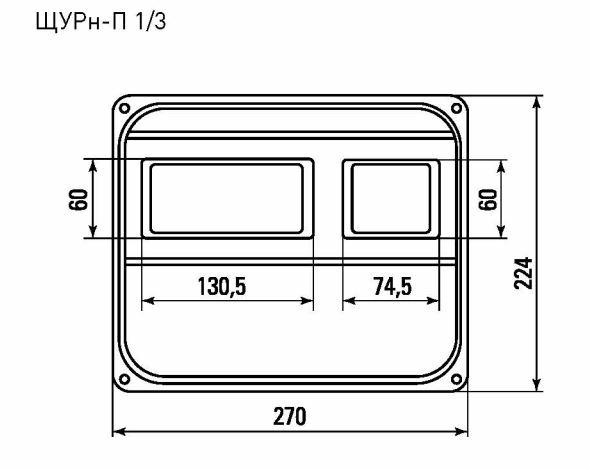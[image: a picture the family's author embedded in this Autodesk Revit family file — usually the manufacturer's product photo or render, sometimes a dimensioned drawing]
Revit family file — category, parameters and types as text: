
# Revit family: EKF_EE_ЦокольУсиленныйFORT_PROxima
name_source: partatom
category: Электрооборудование
units: mm (PartAtom-declared; Revit-internal decimal feet)

## family parameters
Всегда вертикально = Нет
На основе рабочей плоскости = Да
Общий = Да
При загрузке вырезать с полостями = Нет
Размер круглого соединителя = Использовать диаметр
Тип детали = Силовой щит
Точка расчета площади = Нет

## types (12) — shared parameters
ADSK_Единица измерения = шт.
ADSK_Завод-изготовитель = EKF
ADSK_Количество = 1
ADSK_Марка = Цоколь усиленный FORT
ADSK_Материал = RAL 7035_Сталь
ADSK_Обозначение = Цоколь усиленный FORT
ADSK_Размер_Высота = 100 мм
БезСальникПанели = Без сальниковой панели
Глубина = 400 мм
Изготовитель = EKF
КПЦ1000 = EKF_EE_КомплектПанелейЦоколя_FORT_PROxima : Комплект панелей цоколя FORT Ш1000 В200 PROxima (2шт)
КПЦ400 = EKF_EE_КомплектПанелейЦоколя_FORT_PROxima : Комплект панелей цоколя FORT Ш400 В200  PROxima (2шт)
КПЦ600 = EKF_EE_КомплектПанелейЦоколя_FORT_PROxima : Комплект панелей цоколя FORT Ш600 В200 PROxima (2шт)
КПЦ800 = EKF_EE_КомплектПанелейЦоколя_FORT_PROxima : Комплект панелей цоколя FORT  Ш800 В200 PROxima (2 шт)
СальникПанель = EKF_EE_НижняяСальниковаяПанельСоставнаяFORT_PROxima : Нижняя сальниковая панель составная FORT (800x600) EKF PROxima
Серия номенклатуры = PROxima
Степень защиты IP = -
ТВ = EKF_2
Тип установки = -
Ширина = 600 мм
zero-valued in all types: ADSK_Масса, Отметка по умолчанию

## per-type parameters (varying)
| type | ADSK_Код изделия | ADSK_Наименование | ADSK_Размер_Глубина | ADSK_Размер_Ширина | ПанелиЦоколя_Глубина | ПанелиЦоколя_Ширина | СальниковаяПанель | Тип |
| Цоколь усиленный FORT 1000х400 EKF PROxima | FCS104 | Цоколь усиленный FORT 1000х400 EKF PROxima | 400 мм | 1000 мм | EKF_EE_КомплектПанелейЦоколя_FORT_PROxima : Комплект панелей цоколя FORT Ш400 В200  PROxima (2шт) | EKF_EE_КомплектПанелейЦоколя_FORT_PROxima : Комплект панелей цоколя FORT Ш1000 В200 PROxima (2шт) | Без сальниковой панели | 348 мм |
| Цоколь усиленный FORT 1000х600 EKF PROxima | FCS106 | Цоколь усиленный FORT 1000х600 EKF PROxima | 600 мм | 1000 мм | EKF_EE_КомплектПанелейЦоколя_FORT_PROxima : Комплект панелей цоколя FORT Ш600 В200 PROxima (2шт) | EKF_EE_КомплектПанелейЦоколя_FORT_PROxima : Комплект панелей цоколя FORT Ш1000 В200 PROxima (2шт) | Без сальниковой панели | 349 мм |
| Цоколь усиленный FORT 1000х800 EKF PROxima | FCS108 | Цоколь усиленный FORT 1000х800 EKF PROxima | 800 мм | 1000 мм | EKF_EE_КомплектПанелейЦоколя_FORT_PROxima : Комплект панелей цоколя FORT  Ш800 В200 PROxima (2 шт) | EKF_EE_КомплектПанелейЦоколя_FORT_PROxima : Комплект панелей цоколя FORT Ш1000 В200 PROxima (2шт) | Без сальниковой панели | 350 мм |
| Цоколь усиленный FORT 400х400 EKF PROxima | FCS44 | Цоколь усиленный FORT 400х400 EKF PROxima | 400 мм | 400 мм | EKF_EE_КомплектПанелейЦоколя_FORT_PROxima : Комплект панелей цоколя FORT Ш400 В200  PROxima (2шт) | EKF_EE_КомплектПанелейЦоколя_FORT_PROxima : Комплект панелей цоколя FORT Ш400 В200  PROxima (2шт) | Без сальниковой панели | 351 мм |
| Цоколь усиленный FORT 400х600 EKF PROxima | FCS46 | Цоколь усиленный FORT 400х600 EKF PROxima | 600 мм | 400 мм | EKF_EE_КомплектПанелейЦоколя_FORT_PROxima : Комплект панелей цоколя FORT Ш600 В200 PROxima (2шт) | EKF_EE_КомплектПанелейЦоколя_FORT_PROxima : Комплект панелей цоколя FORT Ш400 В200  PROxima (2шт) | Без сальниковой панели | 352 мм |
| Цоколь усиленный FORT 400х800 EKF PROxima | FCS48 | Цоколь усиленный FORT 400х800 EKF PROxima | 800 мм | 400 мм | EKF_EE_КомплектПанелейЦоколя_FORT_PROxima : Комплект панелей цоколя FORT  Ш800 В200 PROxima (2 шт) | EKF_EE_КомплектПанелейЦоколя_FORT_PROxima : Комплект панелей цоколя FORT Ш400 В200  PROxima (2шт) | Без сальниковой панели | 353 мм |
| Цоколь усиленный FORT 600х400 EKF PROxima | FCS64 | Цоколь усиленный FORT 600х400 EKF PROxima | 400 мм | 600 мм | EKF_EE_КомплектПанелейЦоколя_FORT_PROxima : Комплект панелей цоколя FORT Ш400 В200  PROxima (2шт) | EKF_EE_КомплектПанелейЦоколя_FORT_PROxima : Комплект панелей цоколя FORT Ш600 В200 PROxima (2шт) | Без сальниковой панели | 355 мм |
| Цоколь усиленный FORT 600х600 EKF PROxima | FCS66 | Цоколь усиленный FORT 600x600 EKF PROxima | 600 мм | 600 мм | EKF_EE_КомплектПанелейЦоколя_FORT_PROxima : Комплект панелей цоколя FORT Ш600 В200 PROxima (2шт) | EKF_EE_КомплектПанелейЦоколя_FORT_PROxima : Комплект панелей цоколя FORT Ш600 В200 PROxima (2шт) | Без сальниковой панели | 354 мм |
| Цоколь усиленный FORT 600х800 EKF PROxima | FCS68 | Цоколь усиленный FORT 600х800 EKF PROxima | 800 мм | 600 мм | EKF_EE_КомплектПанелейЦоколя_FORT_PROxima : Комплект панелей цоколя FORT  Ш800 В200 PROxima (2 шт) | EKF_EE_КомплектПанелейЦоколя_FORT_PROxima : Комплект панелей цоколя FORT Ш600 В200 PROxima (2шт) | Без сальниковой панели | 356 мм |
| Цоколь усиленный FORT 800х400 EKF PROxima | FCS84 | Цоколь усиленный FORT 800x400 EKF PROxima | 400 мм | 800 мм | EKF_EE_КомплектПанелейЦоколя_FORT_PROxima : Комплект панелей цоколя FORT Ш400 В200  PROxima (2шт) | EKF_EE_КомплектПанелейЦоколя_FORT_PROxima : Комплект панелей цоколя FORT  Ш800 В200 PROxima (2 шт) | Без сальниковой панели | 357 мм |
| Цоколь усиленный FORT 800х600 EKF PROxima | FCS86 | Цоколь усиленный FORT 800x600 EKF PROxima | 600 мм | 800 мм | EKF_EE_КомплектПанелейЦоколя_FORT_PROxima : Комплект панелей цоколя FORT Ш600 В200 PROxima (2шт) | EKF_EE_КомплектПанелейЦоколя_FORT_PROxima : Комплект панелей цоколя FORT  Ш800 В200 PROxima (2 шт) | EKF_EE_НижняяСальниковаяПанельСоставнаяFORT_PROxima : Нижняя сальниковая панель составная FORT (800x600) EKF PROxima | 358 мм |
| Цоколь усиленный FORT 800х800 EKF PROxima | FCS88 | Цоколь усиленный FORT 800х800 EKF PROxima | 800 мм | 800 мм | EKF_EE_КомплектПанелейЦоколя_FORT_PROxima : Комплект панелей цоколя FORT  Ш800 В200 PROxima (2 шт) | EKF_EE_КомплектПанелейЦоколя_FORT_PROxima : Комплект панелей цоколя FORT  Ш800 В200 PROxima (2 шт) | Без сальниковой панели | 359 мм |
